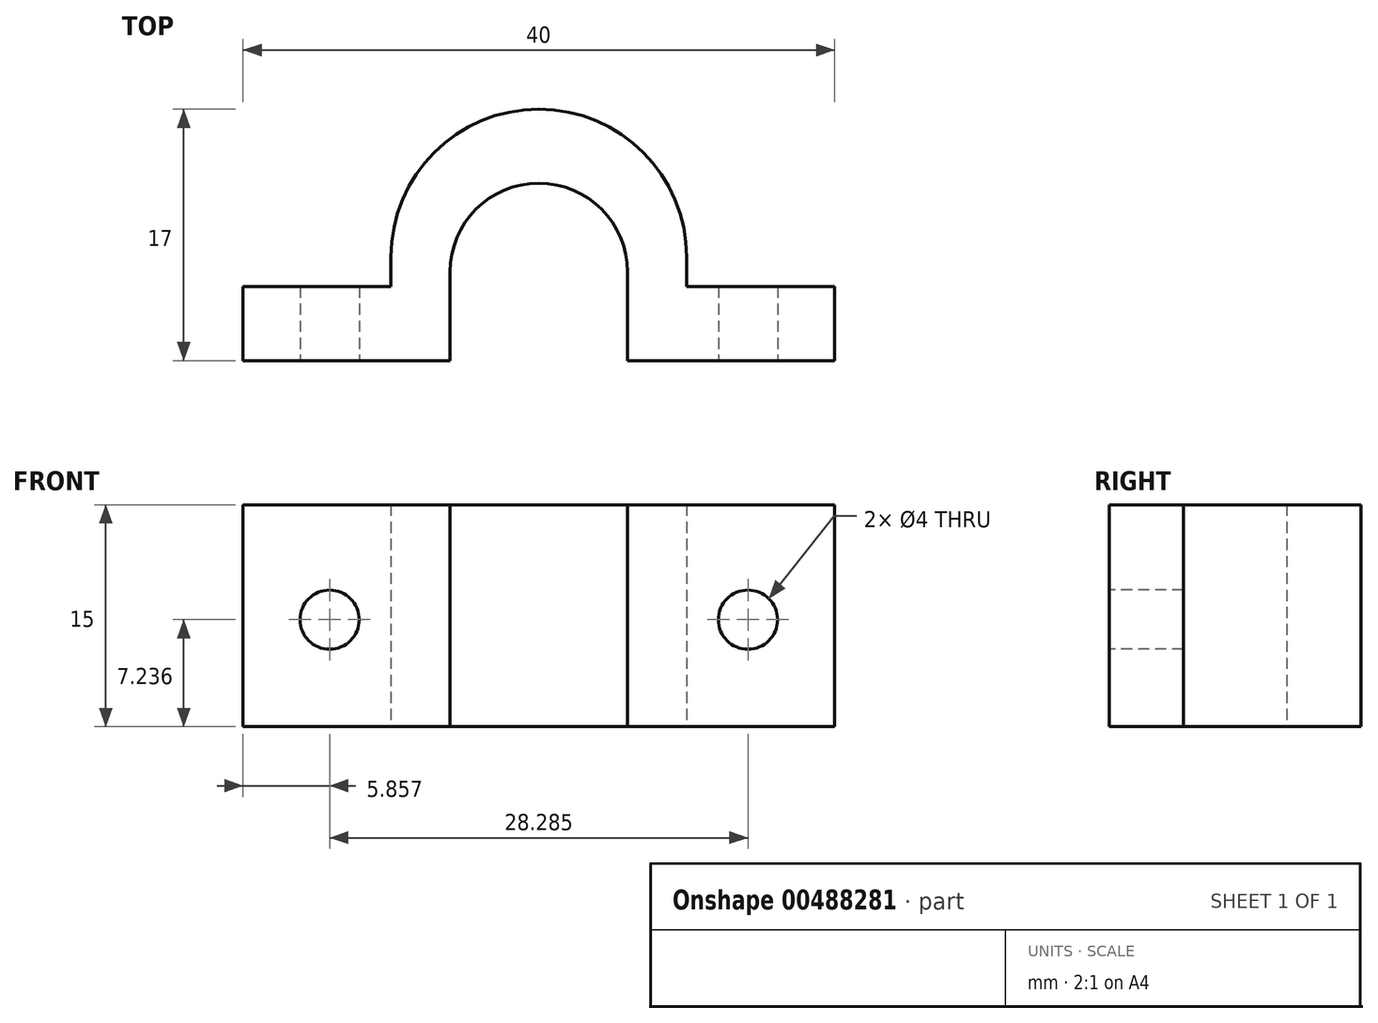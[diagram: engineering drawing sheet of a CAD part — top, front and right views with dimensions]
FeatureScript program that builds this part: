
annotation { "Feature Type Name" : "Feature", "Feature Type Description" : "" }
export const myFeature = defineFeature(function(context is Context, id is Id, definition is map)
    precondition{}
    {
        {
            var Q0;
            Q0=qCreatedBy(makeId("Top.planeOp"),FACE);
            var sketch = newSketch(context, id + "F0", { "sketchPlane" : qUnion([Q0])});
            skLineSegment(sketch, "E0", {"start": v(-10, 7) * mm, "end": v(-10, 5) * mm});
            skLineSegment(sketch, "E1", {"start": v(-10, 5) * mm, "end": v(-20, 5) * mm});
            skLineSegment(sketch, "E2", {"start": v(-20, 5) * mm, "end": v(-20, 0) * mm});
            skLineSegment(sketch, "E3", {"start": v(-20, 0) * mm, "end": v(-6, 0) * mm});
            skLineSegment(sketch, "E4", {"start": v(-6, 0) * mm, "end": v(-6, 6) * mm});
            skLineSegment(sketch, "E5.MirrorCS", {"start": v(20, 0) * mm, "end": v(6, 0) * mm});
            skLineSegment(sketch, "E6.MirrorCS", {"start": v(6, 0) * mm, "end": v(6, 6) * mm});
            skLineSegment(sketch, "E7.MirrorCS", {"start": v(20, 5) * mm, "end": v(20, 0) * mm});
            skLineSegment(sketch, "E8.MirrorCS", {"start": v(10, 7) * mm, "end": v(10, 5) * mm});
            skLineSegment(sketch, "E9.MirrorCS", {"start": v(10, 5) * mm, "end": v(20, 5) * mm});
            skArc(sketch, "E10", {"start": v(6, 6) * mm, "mid": v(0, 12) * mm, "end": v(-6, 6) * mm});
            skArc(sketch, "E11", {"start": v(10, 7) * mm, "mid": v(0, 17) * mm, "end": v(-10, 7) * mm});
            skSolve(sketch);
        }
        {
            var Q0;
            Q0=makeQuery(id+"F0.imprint","IMPRINT",FACE,{"disambiguationData":[TD([[makeQuery(id+"F0.imprint","IMPRINT",EDGE,{"derivedFrom":sQuery(id+"F0.wireOp",EDGE,"E0")}),1.0]])]});
            extrude(context, id + "F1", {"entities" : qUnion([Q0]), "depth" : 15 * mm});
        }
        {
            var Q0;
            Q0=qCreatedBy(makeId("Front.planeOp"),FACE);
            var sketch = newSketch(context, id + "F2", { "sketchPlane" : qUnion([Q0])});
            skCircle(sketch, "E12", {"center": v(-14.14, 7.24) * mm, "radius": 2 * mm});
            skCircle(sketch, "E13.MirrorC", {"center": v(14.14, 7.24) * mm, "radius": 2 * mm});
            skSolve(sketch);
        }
        {
            var Q0;
            Q0 = qSketchRegion(id + "F2", true);
            extrude(context, id + "F3", {"entities" : qUnion([Q0]), "operationType" : NewBodyOperationType.REMOVE, "oppositeDirection" : true, "depth" : 25 * mm});
        }
    });
